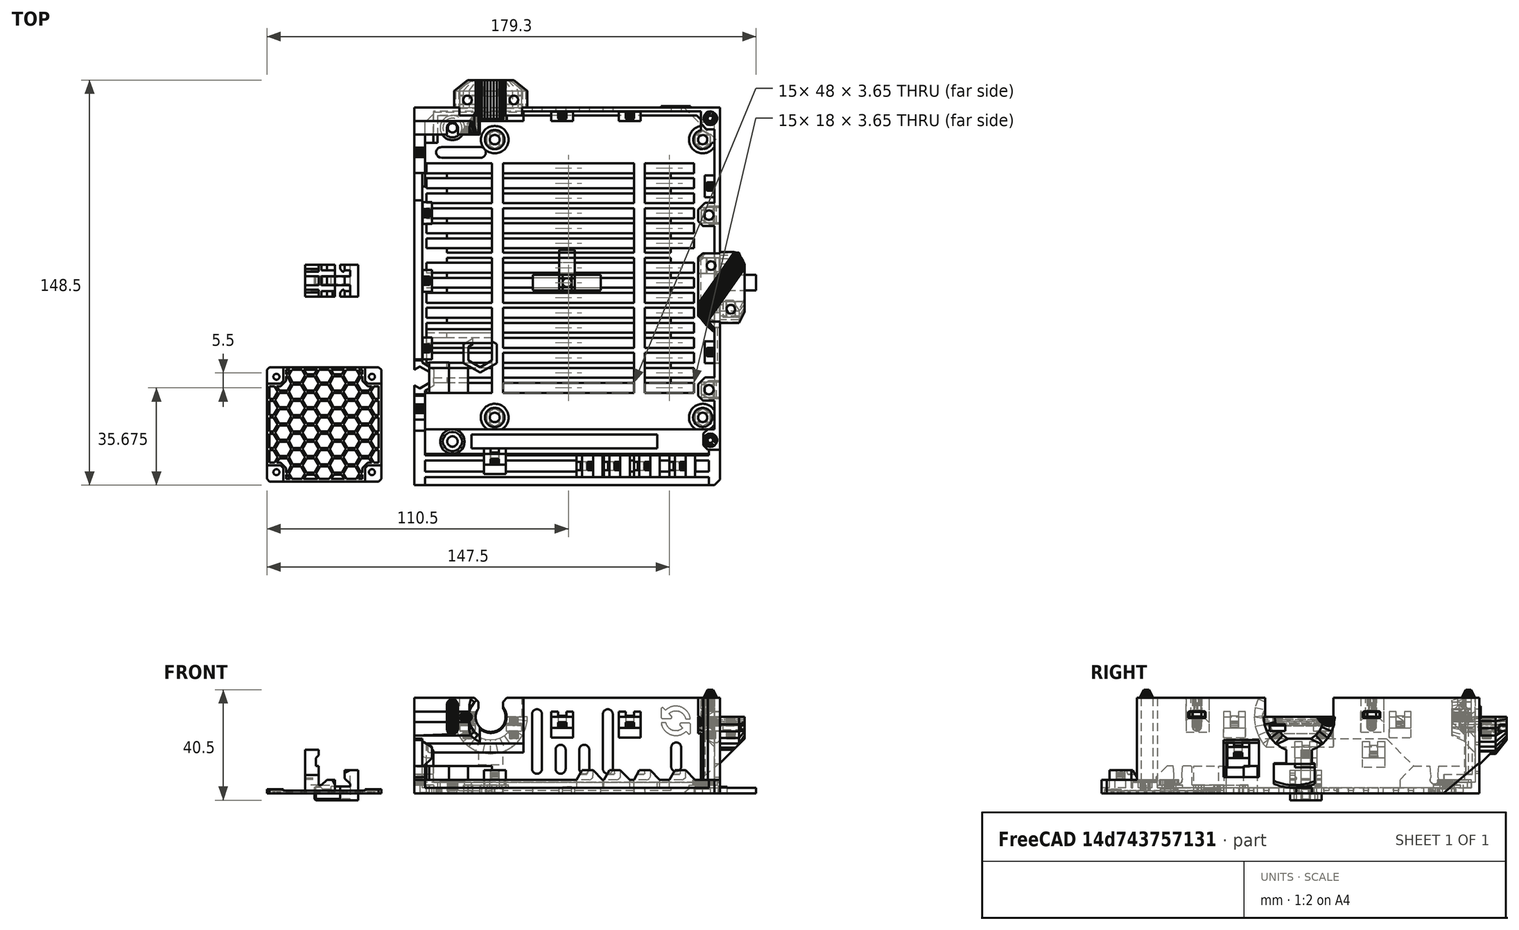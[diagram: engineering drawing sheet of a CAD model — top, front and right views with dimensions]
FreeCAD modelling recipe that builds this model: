
FCSTD DOCUMENT  (FreeCAD 0.18R16146 (Git))
Label: SKR-BASE-universal
License: All rights reserved
LicenseURL: http://en.wikipedia.org/wiki/All_rights_reserved
objects: Part::Box×32, Part::Feature×23, Part::MultiFuse×17, Part::Cut×15, Part::Chamfer×11, Part::Cylinder×3, Part::Cone×1
note: 102 computed .brp shape members not serialized (recipe doc carries the construction recipe); baked Part::Feature solids carry a one-line shape summary decoded from their .brp

FEATURE [Part::Feature] Part__Feature  label="Fusion001005002002006006007006003003004006_(Solid)"
  shape: bbox 121 x 148.5 x 38 mm, 2544 faces (baked)
FEATURE [Part::Feature] Part__Feature001  label="bottom-wire-mounter001_(Solid)"
  Placement = pos=(34,0,0) rot=(0,0,1;0rad)
  shape: bbox 9.5 x 8 x 8.46 mm, 32 faces (baked)
FEATURE [Part::Feature] Part__Feature002  label="bottom-wire-mounter001_(Solid)001"
  Placement = pos=(40.75,-70.25,0) rot=(0,0,-1;1.5708rad)
  shape: bbox 8 x 9.5 x 8.46 mm, 32 faces (baked)
FEATURE [Part::Feature] Part__Feature004  label="bottom-wire-mounter001_(Solid)003"
  Placement = pos=(23,0,0) rot=(0,0,1;0rad)
  shape: bbox 9.5 x 8 x 8.46 mm, 32 faces (baked)
FEATURE [Part::Feature] Part__Feature005  label="bottom-wire-mounter001_(Solid)004"
  Placement = pos=(13,0,0) rot=(0,0,1;0rad)
  shape: bbox 9.5 x 8 x 8.46 mm, 32 faces (baked)
FEATURE [Part::MultiFuse] Fusion
  Shapes = -> [Part__Feature,Part__Feature001]
FEATURE [Part::MultiFuse] Fusion001
  Shapes = -> [Part__Feature005,Fusion]
FEATURE [Part::MultiFuse] Fusion002
  Shapes = -> [Fusion001,Part__Feature004]
FEATURE [Part::Box] Box  label="Cube"
  AttacherType = Attacher::AttachEngine3D
  Height = 6
  Length = 2
  Placement = pos=(54,-12,0) rot=(0,0,1;0rad)
  Width = 17
FEATURE [Part::Cylinder] Cylinder
  Angle = 360
  AttacherType = Attacher::AttachEngine3D
  Height = 10
  Placement = pos=(47,-3.5,22) rot=(0,1,0;1.5708rad)
  Radius = 19
FEATURE [Part::Box] Box001  label="Cube001"
  AttacherType = Attacher::AttachEngine3D
  Height = 24
  Length = 25
  Placement = pos=(-32,49.25,14) rot=(0,0,1;0rad)
  Width = 10
FEATURE [Part::Feature] Part__Feature006  label="bottom-wire-mounter001_(Solid)005"
  Placement = pos=(47,0,0) rot=(0,0,1;0rad)
  shape: bbox 9.5 x 8 x 8.46 mm, 32 faces (baked)
FEATURE [Part::MultiFuse] Fusion003
  Shapes = -> [Fusion002,Part__Feature006]
FEATURE [Part::Cone] Cone
  Angle = 360
  AttacherType = Attacher::AttachEngine3D
  Height = 8
  Placement = pos=(-28,55,28) rot=(-1,0,0;1.5708rad)
  Radius1 = 8
  Radius2 = 4
FEATURE [Part::Box] Box002  label="Cube002"
  AttacherType = Attacher::AttachEngine3D
  Height = 37
  Length = 10
  Placement = pos=(-42,52,0) rot=(0,0,1;0rad)
  Width = 22
FEATURE [Part::Cut] Cut002
  Base = -> Cone
  Tool = -> Box002
FEATURE [Part::Cut] Cut
  Base = -> Box
  Tool = -> Cylinder
FEATURE [Part::Chamfer] Chamfer
  Base = -> Cut
  Edges = 2 edges r=1: [Edge10,Edge11]
FEATURE [Part::Chamfer] Chamfer001
  Base = -> Fusion003
  Edges = 1 edges r=1: [Edge121]
FEATURE [Part::Cut] Cut003
  Base = -> Chamfer001
  Tool = -> Box001
FEATURE [Part::Cut] Cut004
  Base = -> Cut003
  Tool = -> Cut002
FEATURE [Part::MultiFuse] Fusion004
  Shapes = -> [Cut004,Chamfer]
FEATURE [Part::MultiFuse] Fusion005  label="das"
  Shapes = -> [Part__Feature002,Fusion004]
FEATURE [Part::Chamfer] Chamfer002  label="base-rev-3"
  Base = -> Fusion005
  Edges = 60 edges r=0.2: [Edge601,Edge602,Edge603,Edge604,Edge605,Edge665,Edge666,Edge667,Edge668,Edge669,Edge670,Edge711,Edge712,Edge713,Edge714,Edge715,Edge716,Edge717,Edge718,Edge742,Edge743,Edge744,Edge745,Edge746,Edge747,Edge748,Edge749,Edge750,Edge751,Edge752,Edge753,Edge754,Edge755,Edge756,Edge757,Edge758,Edge759,+23 more]
FEATURE [Part::Feature] Chamfer002001_solid  label="Chamfer003 (Solid)"
  shape: bbox 121 x 148.5 x 38 mm, 2747 faces (baked)
FEATURE [Part::Box] Box007  label="reff"
  AttacherType = Attacher::AttachEngine3D
  Height = 2.4
  Length = 5.7
  Placement = pos=(-2.85,-2.85,0) rot=(0,0,1;0rad)
  Width = 5.7
FEATURE [Part::Box] Box008  label="Cube007"
  AttacherType = Attacher::AttachEngine3D
  Height = 0.4
  Length = 10
  Placement = pos=(1.65,-5,2) rot=(0,0,1;0rad)
  Width = 10
FEATURE [Part::Box] Box009  label="Cube008"
  AttacherType = Attacher::AttachEngine3D
  Height = 0.2
  Length = 10
  Placement = pos=(-5,1.65,2.2) rot=(0,0,1;0rad)
  Width = 10
FEATURE [Part::Box] Box010  label="Cube009"
  AttacherType = Attacher::AttachEngine3D
  Height = 0.4
  Length = 10
  Placement = pos=(-11.65,-5,2) rot=(0,0,1;0rad)
  Width = 10
FEATURE [Part::Box] Box011  label="Cube010"
  AttacherType = Attacher::AttachEngine3D
  Height = 0.2
  Length = 10
  Placement = pos=(-5,-11.65,2.2) rot=(0,0,1;0rad)
  Width = 10
FEATURE [Part::Box] Box012  label="reff001"
  AttacherType = Attacher::AttachEngine3D
  Height = 2.4
  Length = 5.7
  Placement = pos=(-2.85,-2.85,0) rot=(0,0,1;0rad)
  Width = 5.7
FEATURE [Part::Box] Box013  label="Cube011"
  AttacherType = Attacher::AttachEngine3D
  Height = 0.2
  Length = 10
  Placement = pos=(1.65,-5,2.2) rot=(0,0,1;0rad)
  Width = 10
FEATURE [Part::Box] Box014  label="Cube012"
  AttacherType = Attacher::AttachEngine3D
  Height = 0.2
  Length = 10
  Placement = pos=(-11.65,-5,2.2) rot=(0,0,1;0rad)
  Width = 10
FEATURE [Part::Box] Box015  label="Cube013"
  AttacherType = Attacher::AttachEngine3D
  Height = 0.4
  Length = 10
  Placement = pos=(-5,-11.65,2) rot=(0,0,1;0rad)
  Width = 10
FEATURE [Part::Box] Box016  label="Cube014"
  AttacherType = Attacher::AttachEngine3D
  Height = 0.4
  Length = 10
  Placement = pos=(-5,1.65,2) rot=(0,0,1;0rad)
  Width = 10
FEATURE [Part::MultiFuse] Fusion006
  Shapes = -> [Box013,Box015,Box014,Box016]
FEATURE [Part::Cylinder] Cylinder001
  Angle = 360
  AttacherType = Attacher::AttachEngine3D
  Height = 10
  Radius = 1.65
FEATURE [Part::MultiFuse] Fusion007
  Shapes = -> [Fusion006,Cylinder001]
FEATURE [Part::Cut] Cut005  label="screw-1"
  Base = -> Box012
  Tool = -> Fusion007
FEATURE [Part::Cylinder] Cylinder002
  Angle = 360
  AttacherType = Attacher::AttachEngine3D
  Height = 10
  Radius = 1.65
FEATURE [Part::MultiFuse] Fusion008
  Shapes = -> [Box008,Box009,Box010,Box011]
FEATURE [Part::MultiFuse] Fusion009
  Shapes = -> [Fusion008,Cylinder002]
FEATURE [Part::Cut] Cut006  label="screw-2"
  Base = -> Box007
  Tool = -> Fusion009
FEATURE [Part::Feature] Cut005002  label="screw-006"
  shape: bbox 5.7 x 5.7 x 2.4 mm, 22 faces (baked)
FEATURE [Part::Box] Box017  label="Cube015"
  AttacherType = Attacher::AttachEngine3D
  Height = 2
  Length = 5.7
  Placement = pos=(-2.85,2,0) rot=(0,0,1;0rad)
  Width = 10
FEATURE [Part::MultiFuse] Fusion010
  Shapes = -> [Box017,Cut005002]
FEATURE [Part::Feature] Fusion010001  label="Fusion011"
  Placement = pos=(-19.5,66.95,23.3) rot=(0,0,1;0rad)
  shape: bbox 5.7 x 14.85 x 2.4 mm, 18 faces (baked)
FEATURE [Part::Feature] Fusion010002  label="Fusion012"
  Placement = pos=(-36.5,66.95,23.3) rot=(0,0,1;0rad)
  shape: bbox 5.7 x 14.85 x 2.4 mm, 18 faces (baked)
FEATURE [Part::Box] Box018  label="Cube016"
  AttacherType = Attacher::AttachEngine3D
  Height = 2
  Length = 10
  Placement = pos=(2.3,-2.85,0) rot=(0,0,1;0rad)
  Width = 5.7
FEATURE [Part::Feature] Cut006001  label="screw-007"
  shape: bbox 5.7 x 5.7 x 2.4 mm, 18 faces (baked)
FEATURE [Part::Feature] Cut006002  label="screw-008"
  shape: bbox 5.7 x 5.7 x 2.4 mm, 18 faces (baked)
FEATURE [Part::Box] Box019  label="Cube017"
  AttacherType = Attacher::AttachEngine3D
  Height = 2
  Length = 10
  Placement = pos=(-12.6,-2.85,0) rot=(0,0,1;0rad)
  Width = 5.7
FEATURE [Part::MultiFuse] Fusion010003
  Shapes = -> [Box019,Cut006002]
FEATURE [Part::MultiFuse] Fusion010004
  Shapes = -> [Cut006001,Box018]
FEATURE [Part::Feature] Fusion010004001  label="Fusion010005"
  Placement = pos=(60,-9.75,23.3) rot=(0,0,1;0rad)
  shape: bbox 15.15 x 5.7 x 2.4 mm, 18 faces (baked)
FEATURE [Part::Feature] Fusion010003001  label="Fusion010006"
  Placement = pos=(52.8,6.25,23.3) rot=(0,0,1;0rad)
  shape: bbox 15.45 x 5.7 x 2.4 mm, 18 faces (baked)
FEATURE [Part::Feature] Fusion010004002  label="Fusion010007"
  Placement = pos=(57,0,0) rot=(0,0,1;0rad)
  shape: bbox 15.15 x 5.7 x 2.4 mm, 18 faces (baked)
FEATURE [Part::Feature] Fusion010004003  label="Fusion010008"
  Placement = pos=(52,24.75,28.05) rot=(0,0,1;0rad)
  shape: bbox 15.15 x 5.7 x 2.4 mm, 18 faces (baked)
FEATURE [Part::Feature] Fusion010004004  label="Fusion010009"
  Placement = pos=(52,-39.25,28.05) rot=(0,0,1;0rad)
  shape: bbox 15.15 x 5.7 x 2.4 mm, 18 faces (baked)
FEATURE [Part::Cut] Cut006003
  Base = -> Chamfer002001_solid
  Tool = -> Fusion010001
FEATURE [Part::Cut] Cut006004
  Base = -> Cut006003
  Tool = -> Fusion010002
FEATURE [Part::Cut] Cut006005
  Base = -> Cut006004
  Tool = -> Fusion010004003
FEATURE [Part::Cut] Cut006006
  Base = -> Cut006005
  Tool = -> Fusion010004004
FEATURE [Part::Cut] Cut006007
  Base = -> Cut006006
  Tool = -> Fusion010004001
FEATURE [Part::Cut] Cut006008
  Base = -> Cut006007
  Tool = -> Fusion010003001
FEATURE [Part::Feature] Body001
  Placement = pos=(-32,-35,0) rot=(0,0,1;0rad)
  shape: bbox 12.12 x 14 x 2 mm, 14 faces (baked)
FEATURE [Part::Feature] Body003
  Placement = pos=(-32,-35,1) rot=(0,0,1;0rad)
  shape: bbox 12.12 x 14 x 2 mm, 14 faces (baked)
FEATURE [Part::MultiFuse] Fusion010004005
  Shapes = -> [Body003,Body001]
FEATURE [Part::Box] Box021  label="Cube019"
  AttacherType = Attacher::AttachEngine3D
  Height = 10
  Length = 14.21
  Placement = pos=(-50.54,-40.4,0) rot=(0,0,1;0rad)
  Width = 9.15
FEATURE [Part::Feature] Body004
  Placement = pos=(-32,-35,0) rot=(0,0,1;0rad)
  shape: bbox 12.12 x 14 x 2 mm, 14 faces (baked)
FEATURE [Part::Box] Box022  label="Cube020"
  AttacherType = Attacher::AttachEngine3D
  Height = 10
  Length = 7.21
  Placement = pos=(-50.54,-40.4,0) rot=(0,0,1;0rad)
  Width = 11.15
FEATURE [Part::MultiFuse] Fusion010004006
  Placement = pos=(0.17,9,0) rot=(0,0,1;0rad)
  Shapes = -> [Fusion010004005,Body004]
FEATURE [Part::Feature] Body002
  Placement = pos=(-32,-26,0) rot=(0,0,1;0rad)
  shape: bbox 10.39 x 12 x 10 mm, 8 faces (baked)
FEATURE [Part::Box] Box023  label="Cube021"
  AttacherType = Attacher::AttachEngine3D
  Height = 10
  Length = 24
  Placement = pos=(-51.5,-22.1,0) rot=(0,0,1;0rad)
  Width = 5
FEATURE [Part::Cut] Cut006009
  Base = -> Cut006008
  Tool = -> Box023
FEATURE [Part::Box] Box020  label="Cube018"
  AttacherType = Attacher::AttachEngine3D
  Height = 10
  Length = 24
  Placement = pos=(-51.5,-22.1,0) rot=(0,0,1;0rad)
  Width = 5
FEATURE [Part::Box] Box024  label="Cube022"
  AttacherType = Attacher::AttachEngine3D
  Height = 10
  Length = 7
  Placement = pos=(-34.5,-25,0) rot=(0,0,1;0rad)
  Width = 10
FEATURE [Part::Cut] Cut006011
  Base = -> Cut006009
  Tool = -> Body002
FEATURE [Part::Cut] Cut006012
  Base = -> Fusion010004006
  Tool = -> Box024
FEATURE [Part::MultiFuse] Fusion010004007
  Shapes = -> [Cut006011,Cut006012]
FEATURE [Part::Box] Box025  label="Cube023"
  AttacherType = Attacher::AttachEngine3D
  Height = 10
  Length = 5
  Placement = pos=(-96,-1,0) rot=(0,0,1;0rad)
  Width = 3.35
FEATURE [Part::Box] Box026  label="Cube024"
  AttacherType = Attacher::AttachEngine3D
  Height = 3
  Length = 11
  Placement = pos=(-96,-5.15,0) rot=(0,0,1;0rad)
  Width = 11.65
FEATURE [Part::Box] Box027  label="Cube025"
  AttacherType = Attacher::AttachEngine3D
  Height = 6
  Length = 5
  Placement = pos=(-96,-5.15,0) rot=(0,0,1;0rad)
  Width = 2
FEATURE [Part::Box] Box028  label="Cube026"
  AttacherType = Attacher::AttachEngine3D
  Height = 6
  Length = 5
  Placement = pos=(-96,4.5,0) rot=(0,0,1;0rad)
  Width = 2
FEATURE [Part::Box] Box030  label="Cube028"
  AttacherType = Attacher::AttachEngine3D
  Height = 1.5
  Length = 5
  Placement = pos=(-96,4,5.2) rot=(0,0,1;0rad)
  Width = 2.5
FEATURE [Part::Box] Box031  label="Cube029"
  AttacherType = Attacher::AttachEngine3D
  Height = 1.5
  Length = 5
  Placement = pos=(-96,-5.15,5.2) rot=(0,0,1;0rad)
  Width = 2.5
FEATURE [Part::Box] Box032  label="Cube030"
  AttacherType = Attacher::AttachEngine3D
  Height = 3
  Length = 4
  Placement = pos=(-96,-1,10) rot=(0,0,1;0rad)
  Width = 3.35
FEATURE [Part::Box] Box033  label="Cube031"
  AttacherType = Attacher::AttachEngine3D
  Height = 3
  Length = 5
  Placement = pos=(-96,0,13) rot=(0,0,1;0rad)
  Width = 3.35
FEATURE [Part::Chamfer] Chamfer005
  Base = -> Box033
  Edges = 1 edges r=1: [Edge8]
  Placement = pos=(0,-1,0) rot=(0,0,1;0rad)
FEATURE [Part::Box] Box034  label="Cube032"
  AttacherType = Attacher::AttachEngine3D
  Height = 5
  Length = 5
  Placement = pos=(-90,-5.15,0) rot=(0,0,1;0rad)
  Width = 2
FEATURE [Part::Box] Box035  label="Cube033"
  AttacherType = Attacher::AttachEngine3D
  Height = 5
  Length = 5
  Placement = pos=(-90,4.5,0) rot=(0,0,1;0rad)
  Width = 2
FEATURE [Part::Box] Box036  label="Cube034"
  AttacherType = Attacher::AttachEngine3D
  Height = 5
  Length = 5
  Placement = pos=(-90,-1,0) rot=(0,0,1;0rad)
  Width = 3.35
FEATURE [Part::Chamfer] Chamfer006
  Base = -> Box030
  Edges = 1 edges r=1: [Edge10]
FEATURE [Part::Chamfer] Chamfer007
  Base = -> Box031
  Edges = 1 edges r=1: [Edge12]
FEATURE [Part::Chamfer] Chamfer008
  Base = -> Box035
  Edges = 1 edges r=2: [Edge2]
FEATURE [Part::Chamfer] Chamfer009
  Base = -> Box036
  Edges = 1 edges r=2: [Edge2]
FEATURE [Part::Chamfer] Chamfer010
  Base = -> Box034
  Edges = 1 edges r=2: [Edge2]
FEATURE [Part::Chamfer] Chamfer011
  Base = -> Chamfer010
  Edges = 1 edges: [Edge15 r1=1 r2=2]
FEATURE [Part::MultiFuse] Fusion010004008
  Shapes = -> [Chamfer011,Chamfer008,Chamfer009,Chamfer006,Box026,Box028,Chamfer005,Box027,Box025,Box032,Chamfer007]
FEATURE [Part::Feature] Fusion010004008001  label="Fusion010004009"
  shape: bbox 11 x 11.65 x 16 mm, 37 faces (baked)
FEATURE [Part::Chamfer] Chamfer012
  Base = -> Fusion010004008001
  Edges = 10 edges r=0.4: [Edge72,Edge74,Edge81,Edge82,Edge83,Edge84,Edge85,Edge86,Edge94,Edge95]
  Placement = pos=(-76.5,0,93.5) rot=(0,-1,0;1.5708rad)
FEATURE [Part::Feature] Cut001001  label="4010-fin"
  Placement = pos=(-89,-52,0) rot=(0,0,1;0rad)
  shape: bbox 42 x 42 x 1.5 mm, 414 faces (baked)
